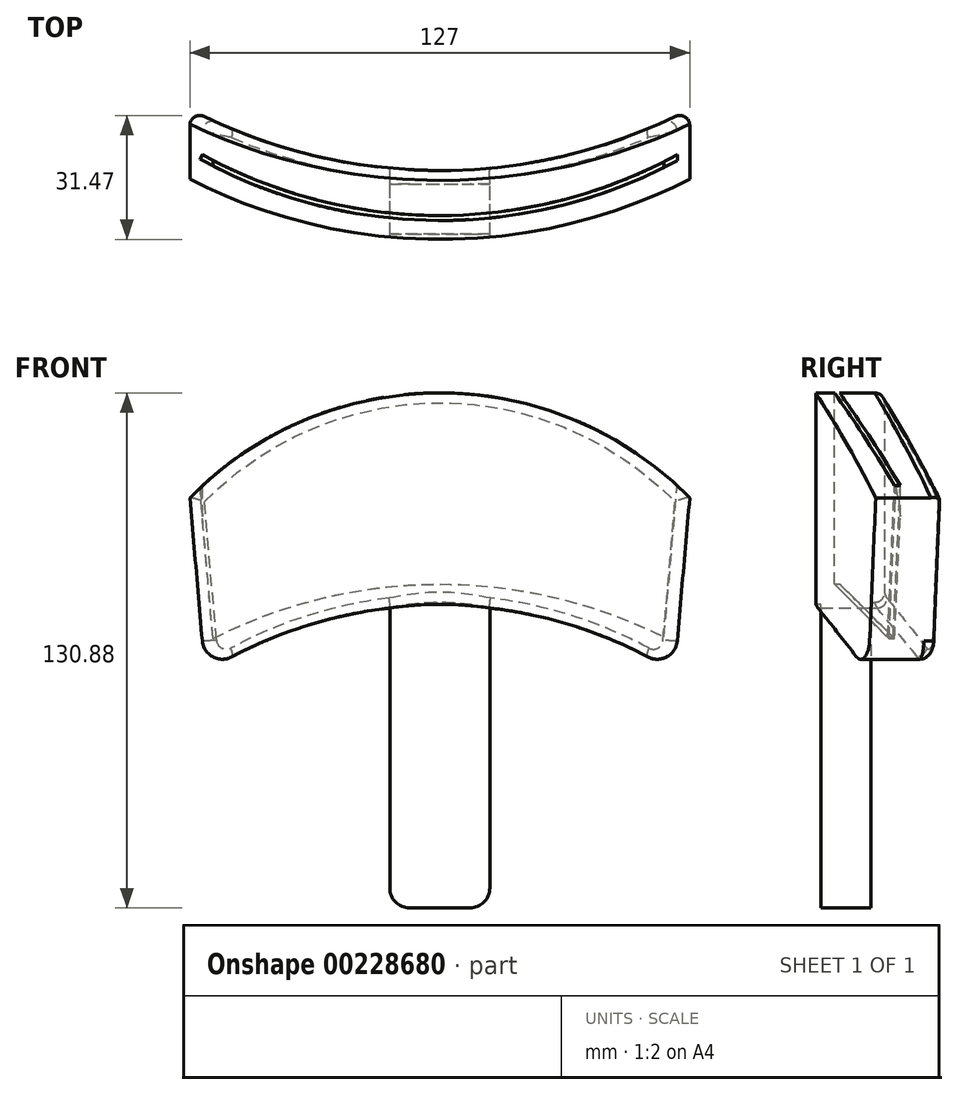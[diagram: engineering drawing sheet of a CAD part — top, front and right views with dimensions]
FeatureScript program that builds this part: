
annotation { "Feature Type Name" : "Feature", "Feature Type Description" : "" }
export const myFeature = defineFeature(function(context is Context, id is Id, definition is map)
    precondition{}
    {
        {
            var Q0;
            Q0=qCreatedBy(makeId("Front.planeOp"),FACE);
            var sketch = newSketch(context, id + "F0", { "sketchPlane" : qUnion([Q0])});
            skArc(sketch, "E0", {"start": v(63.5, 0) * mm, "mid": v(0, 26.68) * mm, "end": v(-63.5, 0) * mm});
            skLineSegment(sketch, "E1", {"start": v(-63.5, 0) * mm, "end": v(0, 0) * mm, "construction": true});
            skLineSegment(sketch, "E2", {"start": v(0, 0) * mm, "end": v(63.5, 0) * mm, "construction": true});
            skLineSegment(sketch, "E3", {"start": v(-63.5, 0) * mm, "end": v(-59.63, -44.28) * mm});
            skLineSegment(sketch, "E4", {"start": v(63.5, 0) * mm, "end": v(59.63, -44.28) * mm});
            skArc(sketch, "E5", {"start": v(59.63, -44.28) * mm, "mid": v(0, -27.28) * mm, "end": v(-59.63, -44.28) * mm});
            skLineSegment(sketch, "E6.bottom", {"start": v(-12.7, -28) * mm, "end": v(12.7, -28) * mm});
            skLineSegment(sketch, "E6.top", {"start": v(-12.7, -104.2) * mm, "end": v(12.7, -104.2) * mm});
            skLineSegment(sketch, "E6.left", {"start": v(-12.7, -28) * mm, "end": v(-12.7, -104.2) * mm});
            skLineSegment(sketch, "E6.right", {"start": v(12.7, -28) * mm, "end": v(12.7, -104.2) * mm});
            skSolve(sketch);
        }
        {
            var Q0;
            Q0 = qSketchRegion(id + "F0", true);
            extrude(context, id + "F1", {"entities" : qUnion([Q0]), "depth" : 44.45 * mm});
        }
        {
            var Q0;
            Q0=makeQuery(id+"F1.opExtrude","CAP_FACE",FACE,{"disambiguationData":[OSD([sQuery(id+"F0.wireOp",EDGE,"E0"),sQuery(id+"F0.wireOp",EDGE,"E3"),sQuery(id+"F0.wireOp",EDGE,"E4"),sQuery(id+"F0.wireOp",EDGE,"E5"),sQuery(id+"F0.wireOp",EDGE,"E6.top"),sQuery(id+"F0.wireOp",EDGE,"E6.left"),sQuery(id+"F0.wireOp",EDGE,"E6.right")])],"isStart":false});
            var sketch = newSketch(context, id + "F2", { "sketchPlane" : qUnion([Q0])});
            skArc(sketch, "E7", {"start": v(12.7, -28) * mm, "mid": v(0, -27.05) * mm, "end": v(-12.7, -28) * mm});
            skLineSegment(sketch, "E8", {"start": v(-12.7, -28) * mm, "end": v(-12.7, -104.2) * mm});
            skLineSegment(sketch, "E9", {"start": v(-12.7, -104.2) * mm, "end": v(12.7, -104.2) * mm});
            skLineSegment(sketch, "E10", {"start": v(12.7, -104.2) * mm, "end": v(12.7, -28) * mm});
            skSolve(sketch);
        }
        {
            var Q0;
            Q0 = qSketchRegion(id + "F2", true);
            extrude(context, id + "F3", {"entities" : qUnion([Q0]), "operationType" : NewBodyOperationType.REMOVE, "oppositeDirection" : true, "depth" : 6.35 * mm});
        }
        {
            var Q0;
            Q0=makeQuery(id+"F1.opExtrude","CAP_FACE",FACE,{"disambiguationData":[OSD([sQuery(id+"F0.wireOp",EDGE,"E0"),sQuery(id+"F0.wireOp",EDGE,"E3"),sQuery(id+"F0.wireOp",EDGE,"E4"),sQuery(id+"F0.wireOp",EDGE,"E5"),sQuery(id+"F0.wireOp",EDGE,"E6.top"),sQuery(id+"F0.wireOp",EDGE,"E6.left"),sQuery(id+"F0.wireOp",EDGE,"E6.right")])],"isStart":true});
            var sketch = newSketch(context, id + "F4", { "sketchPlane" : qUnion([Q0])});
            skArc(sketch, "E11", {"start": v(12.7, -28) * mm, "mid": v(0, -26.56) * mm, "end": v(-12.7, -28) * mm});
            skLineSegment(sketch, "E12", {"start": v(-12.7, -28) * mm, "end": v(-12.7, -104.2) * mm});
            skLineSegment(sketch, "E13", {"start": v(-12.7, -104.2) * mm, "end": v(12.7, -104.2) * mm});
            skLineSegment(sketch, "E14", {"start": v(12.7, -104.2) * mm, "end": v(12.7, -28) * mm});
            skSolve(sketch);
        }
        {
            var Q0;
            Q0 = qSketchRegion(id + "F4", true);
            extrude(context, id + "F5", {"entities" : qUnion([Q0]), "operationType" : NewBodyOperationType.REMOVE, "oppositeDirection" : true, "depth" : 25.4 * mm});
        }
        {
            var Q0;
            Q0=makeQuery(id+"F1.opExtrude","SWEPT_FACE",FACE,{"disambiguationData":[OSD([sQuery(id+"F0.wireOp",EDGE,"E6.top")])]});
            var sketch = newSketch(context, id + "F6", { "sketchPlane" : qUnion([Q0])});
            skArc(sketch, "E15", {"start": v(-63.5, 6.35) * mm, "mid": v(0, 21.92) * mm, "end": v(63.5, 6.35) * mm});
            skLineSegment(sketch, "E16", {"start": v(-63.5, 6.35) * mm, "end": v(-63.5, 0) * mm});
            skLineSegment(sketch, "E17", {"start": v(-63.5, 0) * mm, "end": v(63.5, 0) * mm});
            skLineSegment(sketch, "E18", {"start": v(63.5, 0) * mm, "end": v(63.5, 6.35) * mm});
            skSolve(sketch);
        }
        {
            var Q0;
            Q0=makeQuery(id+"F1.opExtrude","SWEPT_FACE",FACE,{"disambiguationData":[OSD([sQuery(id+"F0.wireOp",EDGE,"E6.top")])]});
            var sketch = newSketch(context, id + "F7", { "sketchPlane" : qUnion([Q0])});
            skArc(sketch, "E19", {"start": v(63.5, 24.16) * mm, "mid": v(0, 39.43) * mm, "end": v(-63.5, 24.16) * mm});
            skLineSegment(sketch, "E20", {"start": v(-63.5, 24.16) * mm, "end": v(-63.5, 50.78) * mm});
            skLineSegment(sketch, "E21", {"start": v(-63.5, 50.78) * mm, "end": v(63.78, 50.78) * mm});
            skLineSegment(sketch, "E22", {"start": v(63.78, 50.78) * mm, "end": v(63.5, 24.16) * mm});
            skSolve(sketch);
        }
        {
            var Q0;
            Q0=makeQuery(id+"F1.opExtrude","SWEPT_FACE",FACE,{"disambiguationData":[OSD([sQuery(id+"F0.wireOp",EDGE,"E6.top")])]});
            cPlane(context, id + "F8", {"entities" : qUnion([Q0]), "cplaneType" : CPlaneType.OFFSET, "offset" : 132.08 * mm, "oppositeDirection" : true, "width" : 152.4 * mm, "height" : 152.4 * mm});
        }
        {
            var Q0;
            Q0=qCreatedBy(id+"F8.planeOp",FACE);
            var sketch = newSketch(context, id + "F9", { "sketchPlane" : qUnion([Q0])});
            skArc(sketch, "E23", {"start": v(60.96, 19.05) * mm, "mid": v(0, 34.64) * mm, "end": v(-60.96, 19.05) * mm});
            skLineSegment(sketch, "E24", {"start": v(-63.5, 19.05) * mm, "end": v(-60.96, 19.05) * mm, "construction": true});
            skLineSegment(sketch, "E25", {"start": v(0, 0) * mm, "end": v(0, 53.93) * mm, "construction": true});
            skLineSegment(sketch, "E26.MirrorCS", {"start": v(63.5, 19.05) * mm, "end": v(60.96, 19.05) * mm, "construction": true});
            skLineSegment(sketch, "E27", {"start": v(-60.96, 19.05) * mm, "end": v(60.96, 19.05) * mm, "construction": true});
            skLineSegment(sketch, "E28", {"start": v(-60.96, 19.05) * mm, "end": v(-60.33, 17.95) * mm});
            skArc(sketch, "E29", {"start": v(0, 33.37) * mm, "mid": v(-31.12, 29.41) * mm, "end": v(-60.33, 17.95) * mm});
            skArc(sketch, "E30.MirrorCS", {"start": v(0, 33.37) * mm, "mid": v(31.12, 29.41) * mm, "end": v(60.33, 17.95) * mm});
            skLineSegment(sketch, "E31.MirrorCS", {"start": v(60.96, 19.05) * mm, "end": v(60.33, 17.95) * mm});
            skSolve(sketch);
        }
        {
            var Q0;
            Q0 = qSketchRegion(id + "F9", true);
            extrude(context, id + "F10", {"entities" : qUnion([Q0]), "operationType" : NewBodyOperationType.REMOVE, "depth" : 69.85 * mm});
        }
        {
            var Q0;
            Q0=makeQuery(id+"F1.opExtrude","CAP_FACE",FACE,{"disambiguationData":[OSD([sQuery(id+"F0.wireOp",EDGE,"E0"),sQuery(id+"F0.wireOp",EDGE,"E3"),sQuery(id+"F0.wireOp",EDGE,"E4"),sQuery(id+"F0.wireOp",EDGE,"E5"),sQuery(id+"F0.wireOp",EDGE,"E6.top"),sQuery(id+"F0.wireOp",EDGE,"E6.left"),sQuery(id+"F0.wireOp",EDGE,"E6.right")])],"isStart":true});
            var sketch = newSketch(context, id + "F11", { "sketchPlane" : qUnion([Q0])});
            skArc(sketch, "E32", {"start": v(57.61, -35.75) * mm, "mid": v(0.37, -21.91) * mm, "end": v(-56.96, -35.4) * mm});
            skLineSegment(sketch, "E33", {"start": v(-56.96, -35.4) * mm, "end": v(-60.33, 3.08) * mm});
            skLineSegment(sketch, "E34", {"start": v(57.61, -35.75) * mm, "end": v(60.96, 2.5) * mm});
            skArc(sketch, "E35", {"start": v(-60.33, 3.08) * mm, "mid": v(-61.93, 1.56) * mm, "end": v(-63.5, 0) * mm});
            skLineSegment(sketch, "E36", {"start": v(-63.5, 0) * mm, "end": v(-59.63, -44.28) * mm});
            skArc(sketch, "E37", {"start": v(-12.7, -28) * mm, "mid": v(-37.07, -33.53) * mm, "end": v(-59.63, -44.28) * mm});
            skArc(sketch, "E38", {"start": v(0, -26.56) * mm, "mid": v(-6.4, -26.92) * mm, "end": v(-12.7, -28) * mm});
            skLineSegment(sketch, "E39", {"start": v(0, 0) * mm, "end": v(0, 17.87) * mm, "construction": true});
            skArc(sketch, "E40.MirrorCS", {"start": v(0, -26.56) * mm, "mid": v(6.4, -26.92) * mm, "end": v(12.7, -28) * mm});
            skArc(sketch, "E41.MirrorCS", {"start": v(12.7, -28) * mm, "mid": v(37.07, -33.53) * mm, "end": v(59.63, -44.28) * mm});
            skLineSegment(sketch, "E42.MirrorCS", {"start": v(63.5, 0) * mm, "end": v(59.63, -44.28) * mm});
            skArc(sketch, "E43.MirrorCS", {"start": v(60.33, 3.08) * mm, "mid": v(61.93, 1.56) * mm, "end": v(63.5, 0) * mm});
            skSolve(sketch);
        }
        {
            var Q0;
            Q0 = qSketchRegion(id + "F11", true);
            extrude(context, id + "F12", {"entities" : qUnion([Q0]), "operationType" : NewBodyOperationType.ADD, "oppositeDirection" : true, "depth" : 44.45 * mm});
        }
        {
            var Q0;
            Q0 = qSketchRegion(id + "F6", true);
            extrude(context, id + "F13", {"entities" : qUnion([Q0]), "operationType" : NewBodyOperationType.REMOVE, "endBound" : BoundingType.THROUGH_ALL, "oppositeDirection" : true, "depth" : 25.4 * mm});
        }
        {
            var Q0;
            Q0 = qSketchRegion(id + "F7", true);
            extrude(context, id + "F14", {"entities" : qUnion([Q0]), "operationType" : NewBodyOperationType.REMOVE, "endBound" : BoundingType.THROUGH_ALL, "oppositeDirection" : true, "depth" : 25.4 * mm});
        }
        {
            var Q0;
            Q0=makeQuery(id+"F5.boolean.opBoolean","COPY",FACE,{"derivedFrom":makeQuery(id+"F5.opExtrude","CAP_FACE",FACE,{"disambiguationData":[OSD([sQuery(id+"F4.wireOp",EDGE,"E11"),sQuery(id+"F4.wireOp",EDGE,"E12"),sQuery(id+"F4.wireOp",EDGE,"E13"),sQuery(id+"F4.wireOp",EDGE,"E14")])],"isStart":false})});
            var sketch = newSketch(context, id + "F15", { "sketchPlane" : qUnion([Q0])});
            skArc(sketch, "E44", {"start": v(12.7, -28) * mm, "mid": v(0, -26.56) * mm, "end": v(-12.7, -28) * mm});
            skLineSegment(sketch, "E45.bottom", {"start": v(-12.7, -28) * mm, "end": v(12.7, -28) * mm});
            skLineSegment(sketch, "E45.top", {"start": v(-12.7, -60.4) * mm, "end": v(12.7, -60.4) * mm});
            skLineSegment(sketch, "E45.left", {"start": v(-12.7, -28) * mm, "end": v(-12.7, -60.4) * mm});
            skLineSegment(sketch, "E45.right", {"start": v(12.7, -28) * mm, "end": v(12.7, -60.4) * mm});
            skSolve(sketch);
        }
        {
            var Q0;
            Q0 = qSketchRegion(id + "F15", true);
            extrude(context, id + "F16", {"entities" : qUnion([Q0]), "operationType" : NewBodyOperationType.ADD, "oppositeDirection" : true, "depth" : 12.7 * mm});
        }
        {
            var Q0;
            Q0=makeQuery(id+"F13.boolean.opBoolean","COPY",FACE,{"derivedFrom":makeQuery(id+"F13.opExtrude","SWEPT_FACE",FACE,{"disambiguationData":[OSD([sQuery(id+"F6.wireOp",EDGE,"E15")])]})});
            fillet(context, id + "F17", {"entities" : qUnion([Q0]), "radius" : 2.54 * mm, "tangentPropagation" : true, "allowEdgeOverflow" : false});
        }
        {
            var Q0;
            Q0=makeQuery(id+"F5.boolean.opBoolean","COPY",EDGE,{"derivedFrom":makeQuery(id+"F5.opExtrude","CAP_EDGE",EDGE,{"disambiguationData":[OSD([sQuery(id+"F4.wireOp",EDGE,"E12")])],"isStart":false})});
            var Q1;
            Q1=makeQuery(id+"F3.boolean.opBoolean","COPY",EDGE,{"derivedFrom":makeQuery(id+"F3.opExtrude","CAP_EDGE",EDGE,{"disambiguationData":[OSD([sQuery(id+"F2.wireOp",EDGE,"E10")])],"isStart":false})});
            var Q2;
            Q2=makeQuery(id+"F3.boolean.opBoolean","COPY",EDGE,{"derivedFrom":makeQuery(id+"F3.opExtrude","CAP_EDGE",EDGE,{"disambiguationData":[OSD([sQuery(id+"F2.wireOp",EDGE,"E8")])],"isStart":false})});
            var Q3;
            Q3=makeQuery(id+"F5.boolean.opBoolean","COPY",EDGE,{"derivedFrom":makeQuery(id+"F5.opExtrude","CAP_EDGE",EDGE,{"disambiguationData":[OSD([sQuery(id+"F4.wireOp",EDGE,"E14")])],"isStart":false})});
            var Q4;
            Q4=makeQuery(id+"F5.boolean.opBoolean","COPY",EDGE,{"derivedFrom":makeQuery(id+"F5.opExtrude","CAP_EDGE",EDGE,{"disambiguationData":[OSD([sQuery(id+"F4.wireOp",EDGE,"E13")])],"isStart":false})});
            var Q5;
            Q5=makeQuery(id+"F1.opExtrude","SWEPT_EDGE",EDGE,{"disambiguationData":[OSD([sQuery(id+"F0.wireOp",EDGE,"E6.top"),sQuery(id+"F0.wireOp",EDGE,"E6.left")])]});
            var Q6;
            Q6=makeQuery(id+"F3.boolean.opBoolean","COPY",EDGE,{"derivedFrom":makeQuery(id+"F3.opExtrude","CAP_EDGE",EDGE,{"disambiguationData":[OSD([sQuery(id+"F2.wireOp",EDGE,"E9")])],"isStart":false})});
            var Q7;
            Q7=makeQuery(id+"F1.opExtrude","SWEPT_EDGE",EDGE,{"disambiguationData":[OSD([sQuery(id+"F0.wireOp",EDGE,"E6.top"),sQuery(id+"F0.wireOp",EDGE,"E6.right")])]});
            fillet(context, id + "F18", {"entities" : qUnion([Q0, Q1, Q2, Q3, Q4, Q5, Q6, Q7]), "radius" : 5.08 * mm, "tangentPropagation" : true, "allowEdgeOverflow" : false});
        }
        {
            var Q0;
            Q0=makeQuery(id+"F1.opExtrude","SWEPT_EDGE",EDGE,{"disambiguationData":[OSD([sQuery(id+"F0.wireOp",EDGE,"E3"),sQuery(id+"F0.wireOp",EDGE,"E5")])]});
            var Q1;
            Q1=makeQuery(id+"F1.opExtrude","SWEPT_EDGE",EDGE,{"disambiguationData":[OSD([sQuery(id+"F0.wireOp",EDGE,"E4"),sQuery(id+"F0.wireOp",EDGE,"E5")])]});
            fillet(context, id + "F19", {"entities" : qUnion([Q0, Q1]), "radius" : 5.08 * mm, "tangentPropagation" : true, "allowEdgeOverflow" : false});
        }
    });
